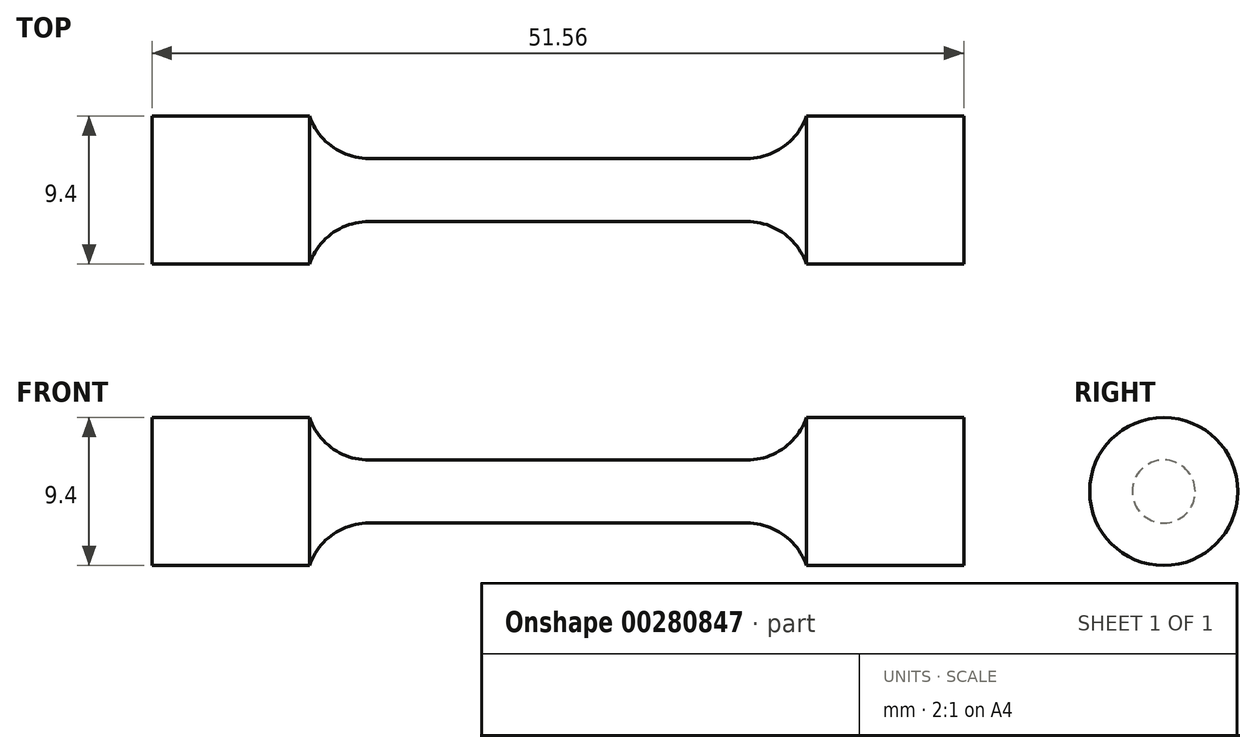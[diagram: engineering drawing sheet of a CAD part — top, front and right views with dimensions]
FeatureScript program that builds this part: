
annotation { "Feature Type Name" : "Feature", "Feature Type Description" : "" }
export const myFeature = defineFeature(function(context is Context, id is Id, definition is map)
    precondition{}
    {
        {
            var Q0;
            Q0=qCreatedBy(makeId("Front.planeOp"),FACE);
            var sketch = newSketch(context, id + "F0", { "sketchPlane" : qUnion([Q0])});
            skLineSegment(sketch, "E0", {"start": v(0, 0) * mm, "end": v(0, 2) * mm});
            skLineSegment(sketch, "E1", {"start": v(0, 2) * mm, "end": v(12, 2) * mm});
            skArc(sketch, "E2", {"start": v(12, 2) * mm, "mid": v(14.32, 2.75) * mm, "end": v(15.78, 4.7) * mm});
            skLineSegment(sketch, "E3", {"start": v(15.78, 4.7) * mm, "end": v(25.78, 4.7) * mm});
            skLineSegment(sketch, "E4", {"start": v(25.78, 4.7) * mm, "end": v(25.78, 0) * mm});
            skArc(sketch, "E5.MirrorCS", {"start": v(-12, 2) * mm, "mid": v(-14.32, 2.75) * mm, "end": v(-15.78, 4.7) * mm});
            skLineSegment(sketch, "E6.MirrorCS", {"start": v(-15.78, 4.7) * mm, "end": v(-25.78, 4.7) * mm});
            skLineSegment(sketch, "E7.MirrorCS", {"start": v(0, 2) * mm, "end": v(-12, 2) * mm});
            skLineSegment(sketch, "E8.MirrorCS", {"start": v(-25.78, 4.7) * mm, "end": v(-25.78, 0) * mm});
            skLineSegment(sketch, "E9", {"start": v(-25.78, 0) * mm, "end": v(25.78, 0) * mm});
            skSolve(sketch);
        }
        {
            var Q0;
            Q0=qSketchRegion(id+"F0",true);
            var Q1;
            Q1=sQuery(id+"F0.wireOp",EDGE,"E9");
            revolve(context, id + "F1", {"entities" : qUnion([Q0]), "axis" : qUnion([Q1]), "revolveType" : RevolveType.FULL});
        }
    });
